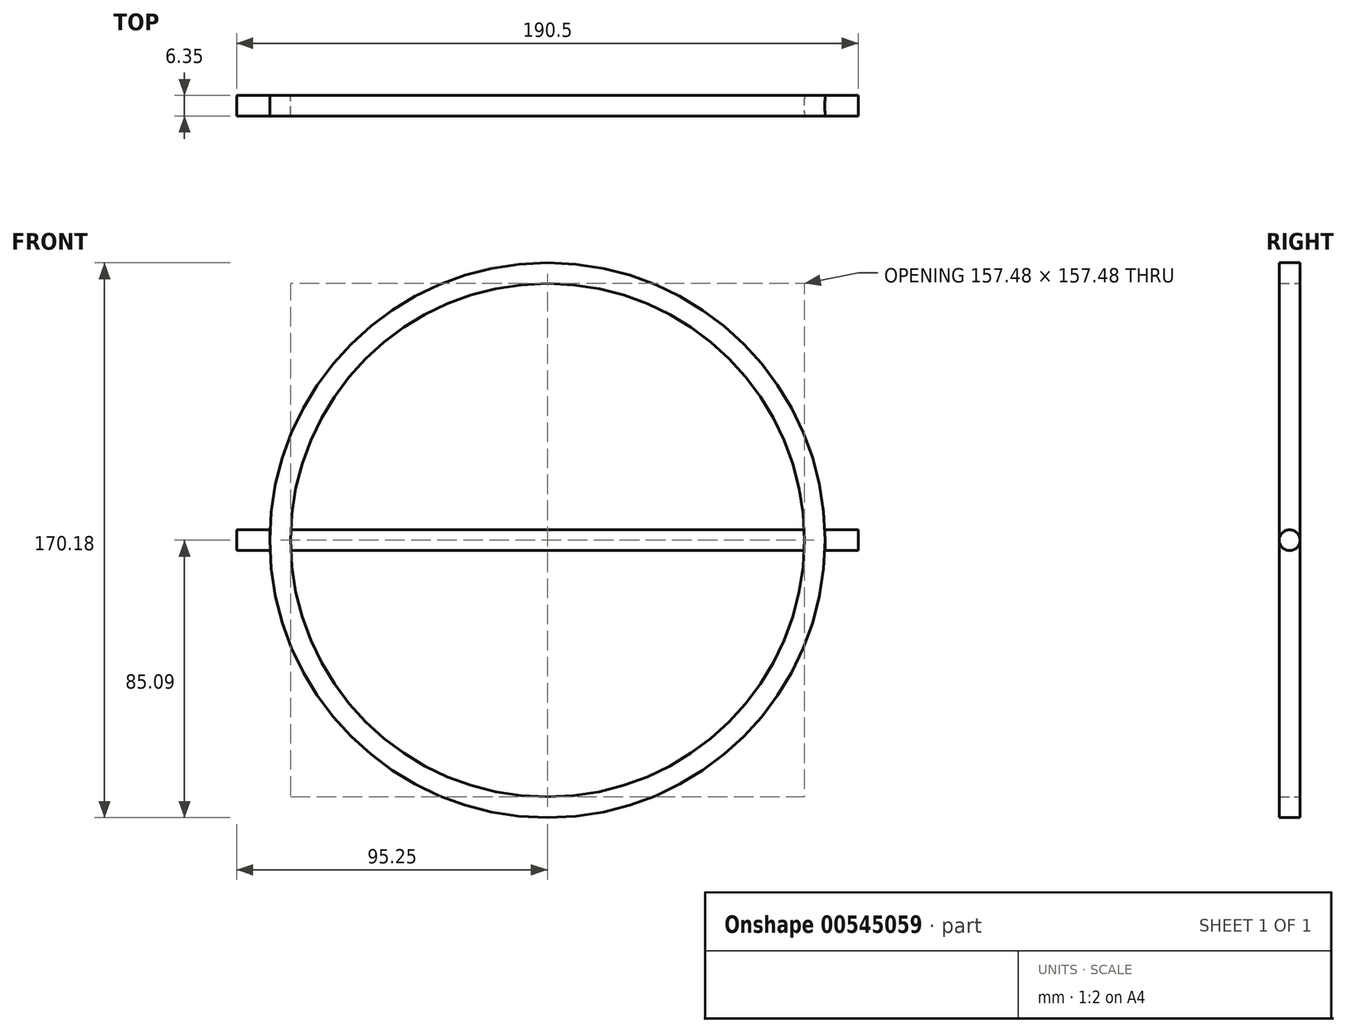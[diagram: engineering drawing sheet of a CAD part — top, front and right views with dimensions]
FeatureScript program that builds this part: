
annotation { "Feature Type Name" : "Feature", "Feature Type Description" : "" }
export const myFeature = defineFeature(function(context is Context, id is Id, definition is map)
    precondition{}
    {
        {
            var Q0;
            Q0=qCreatedBy(makeId("Front.planeOp"),FACE);
            var sketch = newSketch(context, id + "F0", { "sketchPlane" : qUnion([Q0])});
            skCircle(sketch, "E0", {"center": v(0, 0) * mm, "radius": 78.74 * mm});
            skCircle(sketch, "E1.0", {"center": v(0, 0) * mm, "radius": 85.1 * mm});
            skSolve(sketch);
        }
        {
            var Q0;
            Q0=makeQuery(id+"F0.imprint","IMPRINT",FACE,{"disambiguationData":[TD([[makeQuery(id+"F0.imprint","IMPRINT",EDGE,{"derivedFrom":sQuery(id+"F0.wireOp",EDGE,"E0")}),-1.0]])]});
            extrude(context, id + "F1", {"entities" : qUnion([Q0]), "depth" : 6.35 * mm, "offsetDistance" : 25.4 * mm});
        }
        {
            var Q0;
            Q0=qCreatedBy(makeId("Right.planeOp"),FACE);
            var sketch = newSketch(context, id + "F2", { "sketchPlane" : qUnion([Q0])});
            skLineSegment(sketch, "E2", {"start": v(0, 0) * mm, "end": v(-3.18, 0) * mm});
            skCircle(sketch, "E3", {"center": v(-3.18, 0) * mm, "radius": 3.18 * mm});
            skSolve(sketch);
        }
        {
            var Q0;
            Q0=makeQuery(id+"F2.imprint","IMPRINT",FACE,{"disambiguationData":[TD([[makeQuery(id+"F2.imprint","IMPRINT",EDGE,{"derivedFrom":sQuery(id+"F2.wireOp",EDGE,"E3")}),1.0]])]});
            extrude(context, id + "F3", {"entities" : qUnion([Q0]), "operationType" : NewBodyOperationType.ADD, "endBound" : BoundingType.SYMMETRIC, "depth" : 190.5 * mm, "offsetDistance" : 25.4 * mm});
        }
    });
